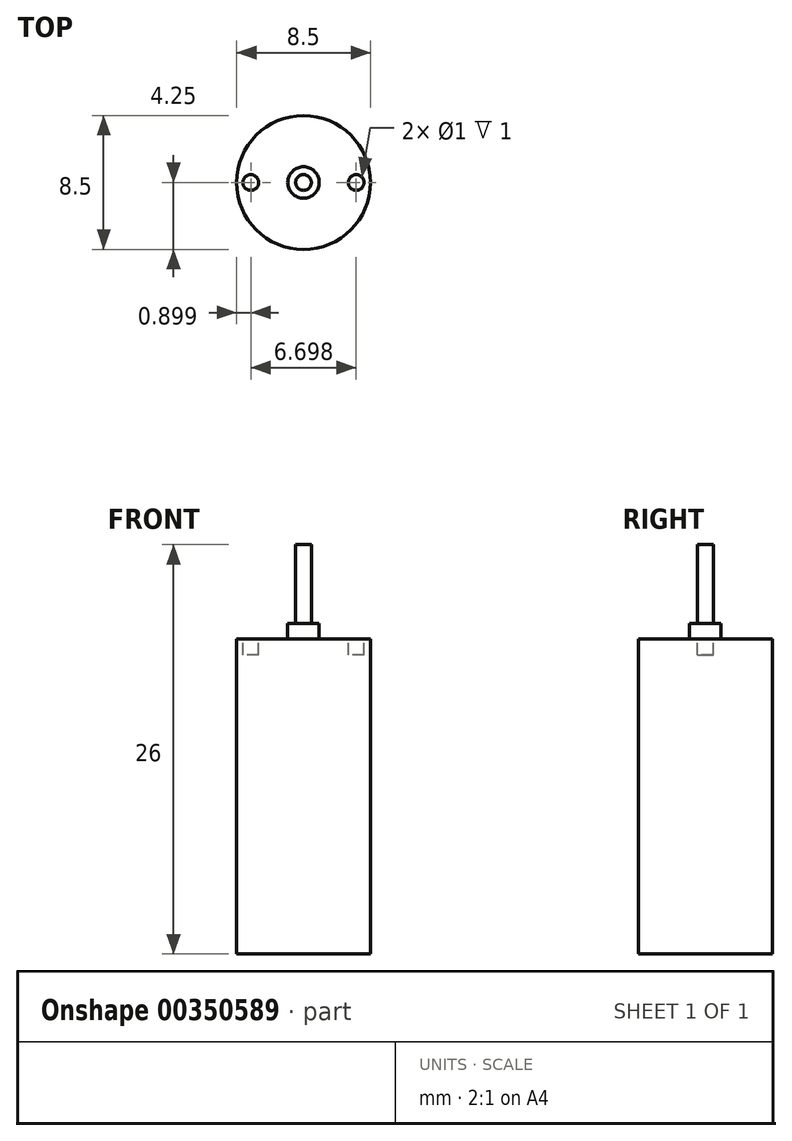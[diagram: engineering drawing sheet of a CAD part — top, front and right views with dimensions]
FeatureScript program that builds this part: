
annotation { "Feature Type Name" : "Feature", "Feature Type Description" : "" }
export const myFeature = defineFeature(function(context is Context, id is Id, definition is map)
    precondition{}
    {
        {
            var Q0;
            Q0=qCreatedBy(makeId("Front.planeOp"),FACE);
            var sketch = newSketch(context, id + "F0", { "sketchPlane" : qUnion([Q0])});
            skLineSegment(sketch, "E0.bottom", {"start": v(-4.64, 12.4) * mm, "end": v(3.86, 12.4) * mm});
            skLineSegment(sketch, "E0.top", {"start": v(-4.64, -7.6) * mm, "end": v(3.86, -7.6) * mm});
            skLineSegment(sketch, "E0.left", {"start": v(-4.64, 12.4) * mm, "end": v(-4.64, -7.6) * mm, "construction": true});
            skLineSegment(sketch, "E0.right", {"start": v(3.86, 12.4) * mm, "end": v(3.86, -7.6) * mm});
            skLineSegment(sketch, "E1.bottom", {"start": v(-0.4, 12.4) * mm, "end": v(-1.4, 12.4) * mm});
            skLineSegment(sketch, "E1.top", {"start": v(-0.4, 13.4) * mm, "end": v(-1.4, 13.4) * mm, "construction": true});
            skLineSegment(sketch, "E1.left", {"start": v(-0.4, 12.4) * mm, "end": v(-0.4, 13.4) * mm});
            skLineSegment(sketch, "E1.right", {"start": v(-1.4, 12.4) * mm, "end": v(-1.4, 13.4) * mm, "construction": true});
            skLineSegment(sketch, "E2", {"start": v(-0.4, -7.6) * mm, "end": v(-0.4, 29.98) * mm, "construction": true});
            skLineSegment(sketch, "E3.bottom", {"start": v(-0.4, 13.4) * mm, "end": v(-0.9, 13.4) * mm});
            skLineSegment(sketch, "E3.top", {"start": v(-0.4, 18.4) * mm, "end": v(-0.9, 18.4) * mm});
            skLineSegment(sketch, "E3.left", {"start": v(-0.4, 13.4) * mm, "end": v(-0.4, 18.4) * mm});
            skLineSegment(sketch, "E3.right", {"start": v(-0.9, 13.4) * mm, "end": v(-0.9, 18.4) * mm, "construction": true});
            skLineSegment(sketch, "E4.MirrorCS", {"start": v(0.6, 12.4) * mm, "end": v(0.6, 13.4) * mm});
            skLineSegment(sketch, "E5.MirrorCS", {"start": v(-0.4, 13.4) * mm, "end": v(0.1, 13.4) * mm});
            skLineSegment(sketch, "E6.MirrorCS", {"start": v(-0.4, 13.4) * mm, "end": v(0.6, 13.4) * mm});
            skLineSegment(sketch, "E7.MirrorCS", {"start": v(0.1, 13.4) * mm, "end": v(0.1, 18.4) * mm});
            skLineSegment(sketch, "E8.MirrorCS", {"start": v(-0.4, 18.4) * mm, "end": v(0.1, 18.4) * mm});
            skLineSegment(sketch, "E9", {"start": v(-0.4, 12.4) * mm, "end": v(-0.4, -7.6) * mm});
            skSolve(sketch);
        }
        {
            var Q0;
            {var subQ0=sQuery(id+"F0.wireOp",EDGE,"E0.right");Q0=makeQuery(id+"F0.imprint","IMPRINT",FACE,{"disambiguationData":[TD([[makeQuery(id+"F0.imprint","IMPRINT",EDGE,{"derivedFrom":subQ0}),-1.0]])]});}
            var Q1;
            {var subQ1=sQuery(id+"F0.wireOp",EDGE,"E1.left");Q1=makeQuery(id+"F0.imprint","IMPRINT",FACE,{"disambiguationData":[TD([[makeQuery(id+"F0.imprint","IMPRINT",EDGE,{"derivedFrom":subQ1}),-1.0]])]});}
            var Q2;
            {var subQ0=sQuery(id+"F0.wireOp",EDGE,"E3.left");Q2=makeQuery(id+"F0.imprint","IMPRINT",FACE,{"disambiguationData":[TD([[makeQuery(id+"F0.imprint","IMPRINT",EDGE,{"derivedFrom":subQ0}),-1.0]])]});}
            var Q3;
            Q3=sQuery(id+"F0.wireOp",EDGE,"E2");
            revolve(context, id + "F1", {"entities" : qUnion([Q0, Q1, Q2]), "axis" : qUnion([Q3]), "revolveType" : RevolveType.FULL});
        }
        {
            var Q0;
            Q0=makeQuery(id+"F1.opRevolve","SWEPT_FACE",FACE,{"disambiguationData":[OSD([sQuery(id+"F0.wireOp",EDGE,"E0.bottom")])]});
            var sketch = newSketch(context, id + "F2", { "sketchPlane" : qUnion([Q0])});
            skLineSegment(sketch, "E10", {"start": v(-9.07, 0) * mm, "end": v(9.62, 0) * mm, "construction": true});
            skLineSegment(sketch, "E11", {"start": v(-0.4, 0) * mm, "end": v(-0.4, 8.75) * mm, "construction": true});
            skLineSegment(sketch, "E12", {"start": v(-0.4, 0) * mm, "end": v(-0.4, -9.34) * mm, "construction": true});
            skLineSegment(sketch, "E13", {"start": v(-4.64, 0) * mm, "end": v(-1.4, 0) * mm});
            skCircle(sketch, "E14", {"center": v(-3.74, 0) * mm, "radius": 0.5 * mm});
            skCircle(sketch, "E15.MirrorC", {"center": v(2.96, 0) * mm, "radius": 0.5 * mm});
            skSolve(sketch);
        }
        {
            var Q0;
            Q0 = qSketchRegion(id + "F2", true);
            extrude(context, id + "F3", {"entities" : qUnion([Q0]), "operationType" : NewBodyOperationType.REMOVE, "oppositeDirection" : true, "depth" : 1 * mm});
        }
    });
